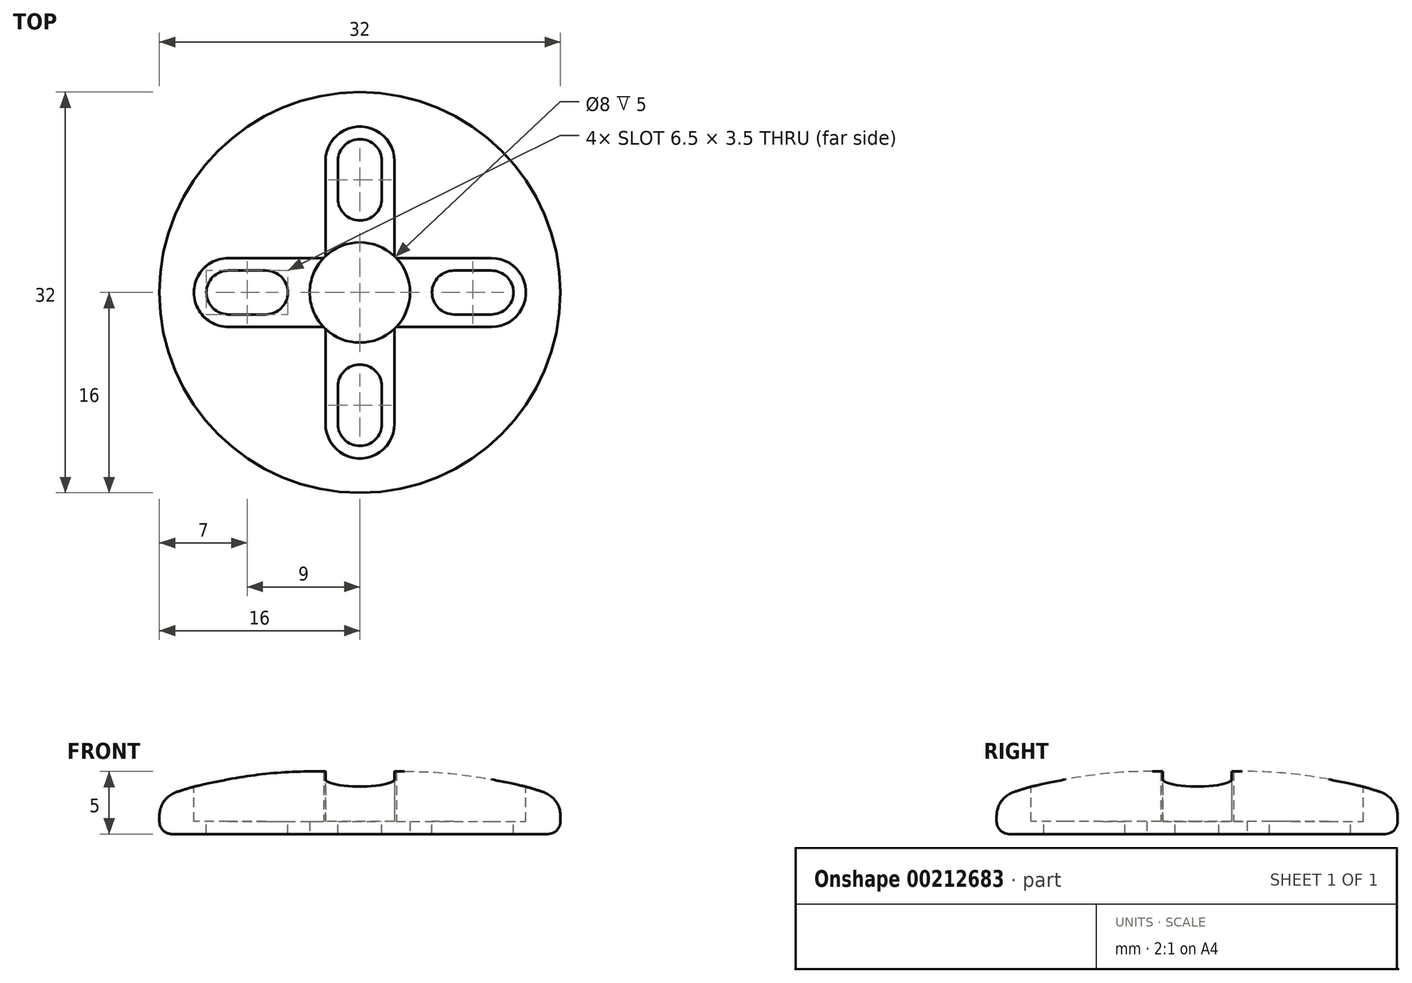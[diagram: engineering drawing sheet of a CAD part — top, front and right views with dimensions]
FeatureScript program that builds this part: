
annotation { "Feature Type Name" : "Feature", "Feature Type Description" : "" }
export const myFeature = defineFeature(function(context is Context, id is Id, definition is map)
    precondition{}
    {
        {
            var Q0;
            Q0=qCreatedBy(makeId("Front.planeOp"),FACE);
            var sketch = newSketch(context, id + "F0", { "sketchPlane" : qUnion([Q0])});
            skLineSegment(sketch, "E0.bottom", {"start": v(4, 0) * mm, "end": v(15, 0) * mm});
            skLineSegment(sketch, "E0.top", {"start": v(4, 5) * mm, "end": v(4.5, 5) * mm});
            skLineSegment(sketch, "E0.left", {"start": v(0, 0) * mm, "end": v(0, 5) * mm, "construction": true});
            skLineSegment(sketch, "E0.right", {"start": v(16, 1) * mm, "end": v(16, 1.46) * mm});
            skArc(sketch, "E1", {"start": v(14.63, 3.35) * mm, "mid": v(9.63, 4.59) * mm, "end": v(4.5, 5) * mm});
            skPoint(sketch, "E2.visualSharp", {"position": v(16, 2.86) * mm});
            skArc(sketch, "E2.filletArc", {"start": v(16, 1.46) * mm, "mid": v(15.62, 2.63) * mm, "end": v(14.63, 3.35) * mm});
            skPoint(sketch, "E3.visualSharp", {"position": v(16, 0) * mm});
            skArc(sketch, "E3.filletArc", {"start": v(15, 0) * mm, "mid": v(15.7, 0.3) * mm, "end": v(16, 1) * mm});
            skLineSegment(sketch, "E4", {"start": v(4, 5) * mm, "end": v(4, 0) * mm});
            skSolve(sketch);
        }
        {
            var Q0;
            Q0 = qSketchRegion(id + "F0", true);
            var Q1;
            Q1=sQuery(id+"F0.wireOp",EDGE,"E0.left");
            revolve(context, id + "F1", {"entities" : qUnion([Q0]), "axis" : qUnion([Q1]), "revolveType" : RevolveType.FULL});
        }
        {
            var Q0;
            Q0=makeQuery(id+"F1.opRevolve","SWEPT_FACE",FACE,{"disambiguationData":[OSD([sQuery(id+"F0.wireOp",EDGE,"E0.top")])]});
            var sketch = newSketch(context, id + "F2", { "sketchPlane" : qUnion([Q0])});
            skLineSegment(sketch, "E5.bottom", {"start": v(-1.75, 10.5) * mm, "end": v(1.75, 10.5) * mm, "construction": true});
            skLineSegment(sketch, "E5.top", {"start": v(-1.75, 7.5) * mm, "end": v(1.75, 7.5) * mm, "construction": true});
            skLineSegment(sketch, "E5.left", {"start": v(-1.75, 10.5) * mm, "end": v(-1.75, 7.5) * mm});
            skLineSegment(sketch, "E5.right", {"start": v(1.75, 10.5) * mm, "end": v(1.75, 7.5) * mm});
            skArc(sketch, "E6", {"start": v(1.75, 10.5) * mm, "mid": v(0, 12.25) * mm, "end": v(-1.75, 10.5) * mm});
            skArc(sketch, "E7", {"start": v(-1.75, 7.5) * mm, "mid": v(0, 5.75) * mm, "end": v(1.75, 7.5) * mm});
            skLineSegment(sketch, "E8.1.0", {"start": v(-10.5, -1.75) * mm, "end": v(-10.5, 1.75) * mm, "construction": true});
            skArc(sketch, "E8.1.1", {"start": v(-10.5, 1.75) * mm, "mid": v(-12.25, 0) * mm, "end": v(-10.5, -1.75) * mm});
            skLineSegment(sketch, "E8.1.2", {"start": v(-10.5, -1.75) * mm, "end": v(-7.5, -1.75) * mm});
            skLineSegment(sketch, "E8.1.3", {"start": v(-10.5, 1.75) * mm, "end": v(-7.5, 1.75) * mm});
            skLineSegment(sketch, "E8.1.4", {"start": v(-7.5, -1.75) * mm, "end": v(-7.5, 1.75) * mm, "construction": true});
            skArc(sketch, "E8.1.5", {"start": v(-7.5, -1.75) * mm, "mid": v(-5.75, 0) * mm, "end": v(-7.5, 1.75) * mm});
            skLineSegment(sketch, "E8.2.0", {"start": v(1.75, -10.5) * mm, "end": v(-1.75, -10.5) * mm, "construction": true});
            skArc(sketch, "E8.2.1", {"start": v(-1.75, -10.5) * mm, "mid": v(0, -12.25) * mm, "end": v(1.75, -10.5) * mm});
            skLineSegment(sketch, "E8.2.2", {"start": v(1.75, -10.5) * mm, "end": v(1.75, -7.5) * mm});
            skLineSegment(sketch, "E8.2.3", {"start": v(-1.75, -10.5) * mm, "end": v(-1.75, -7.5) * mm});
            skLineSegment(sketch, "E8.2.4", {"start": v(1.75, -7.5) * mm, "end": v(-1.75, -7.5) * mm, "construction": true});
            skArc(sketch, "E8.2.5", {"start": v(1.75, -7.5) * mm, "mid": v(0, -5.75) * mm, "end": v(-1.75, -7.5) * mm});
            skLineSegment(sketch, "E8.3.0", {"start": v(10.5, 1.75) * mm, "end": v(10.5, -1.75) * mm, "construction": true});
            skArc(sketch, "E8.3.1", {"start": v(10.5, -1.75) * mm, "mid": v(12.25, 0) * mm, "end": v(10.5, 1.75) * mm});
            skLineSegment(sketch, "E8.3.2", {"start": v(10.5, 1.75) * mm, "end": v(7.5, 1.75) * mm});
            skLineSegment(sketch, "E8.3.3", {"start": v(10.5, -1.75) * mm, "end": v(7.5, -1.75) * mm});
            skLineSegment(sketch, "E8.3.4", {"start": v(7.5, 1.75) * mm, "end": v(7.5, -1.75) * mm, "construction": true});
            skArc(sketch, "E8.3.5", {"start": v(7.5, 1.75) * mm, "mid": v(5.75, 0) * mm, "end": v(7.5, -1.75) * mm});
            skPoint(sketch, "E8.center", {"position": v(0, 0) * mm});
            skSolve(sketch);
        }
        {
            var Q0;
            Q0 = qSketchRegion(id + "F2", true);
            extrude(context, id + "F3", {"entities" : qUnion([Q0]), "operationType" : NewBodyOperationType.REMOVE, "oppositeDirection" : true, "depth" : 25 * mm});
        }
        {
            var Q0;
            Q0=makeQuery(id+"F1.opRevolve","SWEPT_FACE",FACE,{"disambiguationData":[OSD([sQuery(id+"F0.wireOp",EDGE,"E0.top")])]});
            var sketch = newSketch(context, id + "F4", { "sketchPlane" : qUnion([Q0])});
            skArc(sketch, "E9", {"start": v(2.75, 10.5) * mm, "mid": v(0, 13.25) * mm, "end": v(-2.75, 10.5) * mm});
            skLineSegment(sketch, "E10.left", {"start": v(-2.75, 10.5) * mm, "end": v(-2.75, 2.75) * mm});
            skLineSegment(sketch, "E10.right", {"start": v(2.75, 10.5) * mm, "end": v(2.75, 2.75) * mm});
            skArc(sketch, "E11", {"start": v(-2.75, -10.5) * mm, "mid": v(0, -13.25) * mm, "end": v(2.75, -10.5) * mm});
            skArc(sketch, "E12", {"start": v(10.5, -2.75) * mm, "mid": v(13.25, 0) * mm, "end": v(10.5, 2.75) * mm});
            skArc(sketch, "E13", {"start": v(-10.5, 2.75) * mm, "mid": v(-13.25, 0) * mm, "end": v(-10.5, -2.75) * mm});
            skLineSegment(sketch, "E14", {"start": v(-10.5, -2.75) * mm, "end": v(-2.75, -2.75) * mm});
            skLineSegment(sketch, "E15", {"start": v(-10.5, 2.75) * mm, "end": v(-2.75, 2.75) * mm});
            skLineSegment(sketch, "E16.trimOffspring", {"start": v(2.75, -2.75) * mm, "end": v(2.75, -10.5) * mm});
            skLineSegment(sketch, "E17.trimOffspring", {"start": v(-2.75, -2.75) * mm, "end": v(-2.75, -10.5) * mm});
            skLineSegment(sketch, "E18.trimOffspring", {"start": v(2.75, 2.75) * mm, "end": v(10.5, 2.75) * mm});
            skLineSegment(sketch, "E19.trimOffspring", {"start": v(2.75, -2.75) * mm, "end": v(10.5, -2.75) * mm});
            skSolve(sketch);
        }
        {
            var Q0;
            Q0 = qSketchRegion(id + "F4", true);
            extrude(context, id + "F5", {"entities" : qUnion([Q0]), "operationType" : NewBodyOperationType.REMOVE, "oppositeDirection" : true, "depth" : 4 * mm});
        }
    });
